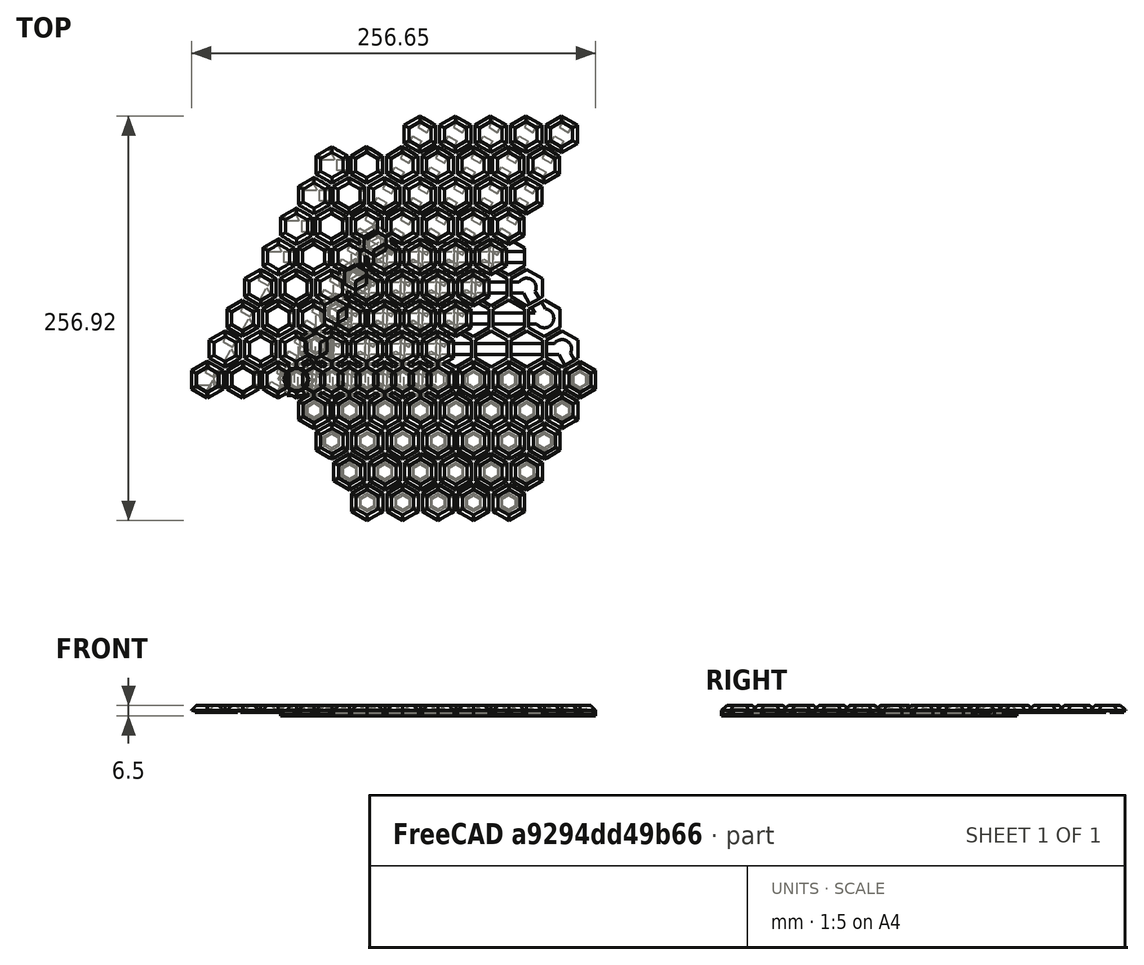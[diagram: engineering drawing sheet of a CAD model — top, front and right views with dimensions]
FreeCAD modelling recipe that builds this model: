
FCSTD DOCUMENT  (FreeCAD 0.21R33771 (Git))
Label: WearableHexLattice
License: All rights reserved
LicenseURL: http://en.wikipedia.org/wiki/All_rights_reserved
objects: Part::FeaturePython×65, Sketcher::SketchObject×16, PartDesign::Pad×12, PartDesign::Body×9, PartDesign::ShapeBinder×6, PartDesign::Pocket×4, Part::Mirroring×4, App::Part×4, PartDesign::FeatureBase×2, Part::Compound×2, Part::MultiFuse×1, Part::Box×1, Part::Cut×1, Mesh::Feature×1, TechDraw::DrawSVGTemplate×1, TechDraw::DrawViewPart×1, TechDraw::DrawPage×1, Spreadsheet::Sheet×1
note: 139 computed .brp shape members not serialized (recipe doc carries the construction recipe); baked Part::Feature solids carry a one-line shape summary decoded from their .brp

FEATURE [Sketcher::SketchObject] Sketch
  FullyConstrained = true
  MapMode = 5
  expr: Constraints[19] = 10 mm * 2 / sqrt(3)
  sketch-geometry (7):
    g0: LineSegment StartX=-11.547 StartY=0 StartZ=0 EndX=-5.7735 EndY=-10 EndZ=0
    g1: LineSegment StartX=-5.7735 StartY=-10 StartZ=0 EndX=5.7735 EndY=-10 EndZ=0
    g2: LineSegment StartX=5.7735 StartY=-10 StartZ=0 EndX=11.547 EndY=1.41807e-11 EndZ=0
    g3: LineSegment StartX=11.547 StartY=1.41807e-11 StartZ=0 EndX=5.7735 EndY=10 EndZ=0
    g4: LineSegment StartX=5.7735 StartY=10 StartZ=0 EndX=-5.7735 EndY=10 EndZ=0
    g5: LineSegment StartX=-5.7735 StartY=10 StartZ=0 EndX=-11.547 EndY=0 EndZ=0
    g6: Circle CenterX=0 CenterY=0 CenterZ=0 NormalX=0 NormalY=0 NormalZ=1 AngleXU=0 Radius=11.547
  constraints (16):
    c: Coincident(g0,g1)
    c: Coincident(g1,g2)
    c: Coincident(g2,g3)
    c: Coincident(g3,g4)
    c: Coincident(g4,g5)
    c: Coincident(g5,g0)
    c: Equal(g0, g1-g5) x5
    c: PointOnObject(g0,g6)
    c: PointOnObject(g1,g6)
    c: PointOnObject(g2,g6)
    c: PointOnObject(g3,g6)
    c: PointOnObject(g4,g6)
    c: PointOnObject(g5,g6)
    c: Coincident(g6,g-1)
    c: PointOnObject(g5,g-1)
    c: DistanceX(g4,g4) = 11.547
FEATURE [PartDesign::Pad] Pad
  Direction = (0,0,1)
  Length = 3
  Length2 = 10
  Profile = -> Sketch
  ReferenceAxis = -> Sketch [N_Axis]
  TaperAngle = -45
  Type = 0
FEATURE [PartDesign::Pad] Pad001
  BaseFeature = -> Pad
  Direction = (0,0,1)
  Length = 3.5
  Length2 = 10
  Profile = -> Sketch
  ReferenceAxis = -> Sketch [N_Axis]
  Reversed = true
  Type = 0
FEATURE [Part::MultiFuse] Fusion
  Placement = pos=(0,0,0) rot=(0,0,1;0.523599rad)
  Shapes = -> [Pad001,Pad]
FEATURE [PartDesign::FeatureBase] BaseFeature
  BaseFeature = -> Fusion
FEATURE [Sketcher::SketchObject] Sketch002
  AttachmentOffset = pos=(0,0,-2) rot=(0,0,1;0.523599rad)
  FullyConstrained = true
  MapMode = 5
  Placement = pos=(0,0,-2) rot=(0,0,1;0.523599rad)
  Support = -> [XY_Plane]
  sketch-geometry (7):
    g0: LineSegment StartX=0 StartY=8 StartZ=0 EndX=-6.9282 EndY=4 EndZ=0
    g1: LineSegment StartX=-6.9282 StartY=4 StartZ=0 EndX=-6.9282 EndY=-4 EndZ=0
    g2: LineSegment StartX=-6.9282 StartY=-4 StartZ=0 EndX=0 EndY=-8 EndZ=0
    g3: LineSegment StartX=0 StartY=-8 StartZ=0 EndX=6.9282 EndY=-4 EndZ=0
    g4: LineSegment StartX=6.9282 StartY=-4 StartZ=0 EndX=6.9282 EndY=4 EndZ=0
    g5: LineSegment StartX=6.9282 StartY=4 StartZ=0 EndX=0 EndY=8 EndZ=0
    g6: Circle CenterX=0 CenterY=0 CenterZ=0 NormalX=0 NormalY=0 NormalZ=1 AngleXU=0 Radius=8
  constraints (16):
    c: Coincident(g0,g1)
    c: Coincident(g1,g2)
    c: Coincident(g2,g3)
    c: Coincident(g3,g4)
    c: Coincident(g4,g5)
    c: Coincident(g5,g0)
    c: Equal(g0, g1-g5) x5
    c: PointOnObject(g0,g6)
    c: PointOnObject(g1,g6)
    c: PointOnObject(g2,g6)
    c: PointOnObject(g3,g6)
    c: PointOnObject(g4,g6)
    c: PointOnObject(g5,g6)
    c: Coincident(g6,g-1)
    c: PointOnObject(g5,g-2)
    c: DistanceY(g4,g4) = 8
FEATURE [PartDesign::Pocket] Pocket
  BaseFeature = -> BaseFeature
  Direction = (0,0,-1)
  Length = 3
  Length2 = 5
  Profile = -> Sketch002
  ReferenceAxis = -> Sketch002 [N_Axis]
  Reversed = true
  TaperAngle = -45
  Type = 0
FEATURE [PartDesign::Body] Body  label="Cell"
  BaseFeature = -> Fusion
  Group = -> [BaseFeature,Sketch,Sketch002,Pocket]
  Origin = -> Origin
  Tip = -> Pocket
FEATURE [Sketcher::SketchObject] Sketch001
  FullyConstrained = true
  MapMode = 2
  Support = -> [Body]
  sketch-geometry (15):
    g0: LineSegment StartX=180 StartY=-1.42e-14 StartZ=0 EndX=135 EndY=77.9423 EndZ=0
    g1: LineSegment StartX=135 StartY=77.9423 StartZ=0 EndX=45 EndY=77.9423 EndZ=0
    g2: LineSegment StartX=45 StartY=77.9423 StartZ=0 EndX=0 EndY=0 EndZ=0
    g3: LineSegment StartX=0 StartY=0 StartZ=0 EndX=45 EndY=-77.9423 EndZ=0
    g4: LineSegment StartX=45 StartY=-77.9423 StartZ=0 EndX=135 EndY=-77.9423 EndZ=0
    g5: LineSegment StartX=135 StartY=-77.9423 StartZ=0 EndX=180 EndY=-1.42e-14 EndZ=0
    g6: Circle CenterX=90 CenterY=-1.59e-14 CenterZ=0 NormalX=0 NormalY=0 NormalZ=1 AngleXU=0 Radius=90
    g7: LineSegment StartX=33.75 StartY=58.4567 StartZ=0 EndX=146.25 EndY=58.4567 EndZ=0
    g8: LineSegment StartX=22.5 StartY=38.9711 StartZ=0 EndX=157.5 EndY=38.9711 EndZ=0
    g9: LineSegment StartX=11.25 StartY=19.4856 StartZ=0 EndX=168.75 EndY=19.4856 EndZ=0
    g10: LineSegment StartX=45 StartY=77.9423 StartZ=0 EndX=33.75 EndY=58.4567 EndZ=0
    g11: LineSegment StartX=33.75 StartY=58.4567 StartZ=0 EndX=22.5 EndY=38.9711 EndZ=0
    g12: LineSegment StartX=22.5 StartY=38.9711 StartZ=0 EndX=11.25 EndY=19.4856 EndZ=0
    g13: LineSegment StartX=0 StartY=0 StartZ=0 EndX=180 EndY=-1.42e-14 EndZ=0
    g14: LineSegment StartX=11.25 StartY=19.4856 StartZ=0 EndX=0 EndY=0 EndZ=0
  constraints (39):
    c: Coincident(g0,g1)
    c: Coincident(g1,g2)
    c: Coincident(g2,g3)
    c: Coincident(g3,g4)
    c: Coincident(g4,g5)
    c: Coincident(g5,g0)
    c: Equal(g0, g1-g5) x5
    c: PointOnObject(g0,g6)
    c: PointOnObject(g1,g6)
    c: PointOnObject(g2,g6)
    c: PointOnObject(g3,g6)
    c: PointOnObject(g4,g6)
    c: PointOnObject(g5,g6)
    c: Horizontal(g1)
    c: DistanceX(g1,g1) = 90
    c: PointOnObject(g3,g-2)
    c: PointOnObject(g3,g-1)
    c: PointOnObject(g7,g2)
    c: PointOnObject(g7,g0)
    c: Horizontal(g7)
    c: PointOnObject(g8,g2)
    c: PointOnObject(g8,g0)
    c: Horizontal(g8)
    c: PointOnObject(g9,g2)
    c: PointOnObject(g9,g0)
    c: Horizontal(g9)
    c: Coincident(g10,g1)
    c: Coincident(g10,g7)
    c: Coincident(g11,g7)
    c: Coincident(g11,g8)
    c: Coincident(g12,g8)
    c: Coincident(g12,g9)
    c: Equal(g10,g11)
    c: Equal(g11,g12)
    c: Coincident(g13,g2)
    c: Coincident(g13,g0)
    c: Coincident(g14,g9)
    c: Coincident(g14,g2)
    c: Equal(g12,g14)
FEATURE [Part::Box] Box001  label="Cube"
  AttacherType = Attacher::AttachEngine3D
  Height = 2.5
  Length = 8
  Placement = pos=(-4,-10,-2.5) rot=(0,0,1;0rad)
  Support = -> [XY_Plane]
  Width = 20
FEATURE [Part::FeaturePython] Array  # Draft array (typed FeaturePython)
  AlwaysSyncPlacement = false
  Angle = 120
  ArrayType = 1
  Axis = (0,0,1)
  Base = -> Box001
  Center = (0,0,0)
  Count = 3
  ExpandArray = false
  Fuse = true
  IntervalAxis = (0,0,0)
  IntervalX = (50,0,0)
  IntervalY = (0,50,0)
  IntervalZ = (0,0,50)
  NumberCircles = 3
  NumberPolar = 3
  NumberX = 2
  NumberY = 2
  NumberZ = 1
  PlacementList = 3 placements: [(-4,-10,-2.5),(6.66025,-8.4641,-2.5),(10.6603,1.5359,-2.5)]
  RadialDistance = 50
  ScaleList = (3) [(1,1,1),(1,1,1),(1,1,1)]
  Symmetry = 1
  TangentialDistance = 25
FEATURE [Part::Cut] Cut
  Base = -> Body
  Placement = pos=(0,0,0) rot=(0,0,1;0.523599rad)
  Refine = true
  Tool = -> Array
FEATURE [Part::FeaturePython] Clone  label="Cell001"  # Draft clone (typed FeaturePython)
  AttacherType = Attacher::AttachEngine3D
  Fuse = false
  Objects = -> [Cut]
  Placement = pos=(12.5,21.6506,0) rot=(0,0,1;0.523599rad)
  Scale = (1,1,1)
  expr: .Placement.Base.x = 25 / 2
  expr: .Placement.Base.y = 25 * sqrt(3) / 2
FEATURE [Part::FeaturePython] Clone001  label="Cell002"  # Draft clone (typed FeaturePython)
  AttacherType = Attacher::AttachEngine3D
  Fuse = false
  Objects = -> [Cut]
  Placement = pos=(25,43.3013,0) rot=(0,0,1;0.523599rad)
  Scale = (1,1,1)
  expr: .Placement.Base.x = 50 / 2
  expr: .Placement.Base.y = 50 * sqrt(3) / 2
FEATURE [Part::FeaturePython] Clone002  label="Cell003"  # Draft clone (typed FeaturePython)
  AttacherType = Attacher::AttachEngine3D
  Fuse = false
  Objects = -> [Cut]
  Placement = pos=(37.5,64.9519,0) rot=(0,0,1;0.523599rad)
  Scale = (1,1,1)
  expr: .Placement.Base.x = 75 / 2
  expr: .Placement.Base.y = 75 * sqrt(3) / 2
FEATURE [Part::FeaturePython] Clone003  label="Cell004"  # Draft clone (typed FeaturePython)
  AttacherType = Attacher::AttachEngine3D
  Fuse = false
  Objects = -> [Cut]
  Placement = pos=(50,86.6025,0) rot=(0,0,1;0.523599rad)
  Scale = (1,1,1)
  expr: .Placement.Base.x = 100 / 2
  expr: .Placement.Base.y = 100 * sqrt(3) / 2
FEATURE [Part::FeaturePython] PathArray004  # WARN: FeaturePython — macro-defined, semantics opaque (R4)
  Align = false
  AlignMode = 0
  Base = -> Cut
  Count = 9
  EndOffset = 0
  ExtraTranslation = (0,0,0)
  ForceVertical = false
  PathObject = -> Sketch001
  PathSubelements = -> [Sketch001]
  StartOffset = 0
  TangentVector = (1,0,0)
  VerticalVector = (0,0,1)
FEATURE [Mesh::Feature] Mesh005
FEATURE [TechDraw::DrawSVGTemplate] Template
  EditableTexts = Designed_by_Name=Designed by Name; Drawing_number=Drawing number; FC-Date=Date; FC-SC=Scale; FC-SH=Sheet; FC-Title=Title; Subtitle=Subtitle; Weight=Weight
  Height = 210
  Orientation = 1
  Template = C:/Program Files/FreeCAD 0.21/data/Mod/TechDraw/Templates/A4_LandscapeTD.svg
  Width = 297
FEATURE [Part::FeaturePython] Clone004  label="Cut001"  # Draft clone (typed FeaturePython)
  AttacherType = Attacher::AttachEngine3D
  Fuse = false
  Objects = -> [Cut]
  Placement = pos=(0,0,0) rot=(0,0,1;0.523599rad)
  Scale = (1,1,1)
FEATURE [Part::FeaturePython] PathArray  # WARN: FeaturePython — macro-defined, semantics opaque (R4)
  Align = false
  AlignMode = 0
  Base = -> Clone004
  Count = 5
  EndOffset = 0
  ExtraTranslation = (0,0,0)
  ForceVertical = false
  PathObject = -> Sketch001
  PathSubelements = -> [Sketch001]
  StartOffset = 0
  TangentVector = (1,0,0)
  VerticalVector = (0,0,1)
FEATURE [Part::Mirroring] Part__Mirroring  label="PathArray (Mirror #1)"
  Base = (0,0,0)
  Normal = (0,1,0)
  Source = -> PathArray
FEATURE [Part::FeaturePython] Clone005  label="Cut002"  # Draft clone (typed FeaturePython)
  AttacherType = Attacher::AttachEngine3D
  Fuse = false
  Objects = -> [Cut]
  Placement = pos=(0,0,0) rot=(0,0,1;0.523599rad)
  Scale = (1,1,1)
FEATURE [Part::FeaturePython] PathArray001  # WARN: FeaturePython — macro-defined, semantics opaque (R4)
  Align = false
  AlignMode = 0
  Base = -> Clone005
  Count = 6
  EndOffset = 0
  ExtraTranslation = (0,0,0)
  ForceVertical = false
  PathObject = -> Sketch001
  PathSubelements = -> [Sketch001]
  StartOffset = 0
  TangentVector = (1,0,0)
  VerticalVector = (0,0,1)
FEATURE [Part::Mirroring] Part__Mirroring001  label="PathArray001 (Mirror #2)"
  Base = (0,0,0)
  Normal = (0,1,0)
  Source = -> PathArray001
FEATURE [Part::FeaturePython] Clone006  label="Cut003"  # Draft clone (typed FeaturePython)
  AttacherType = Attacher::AttachEngine3D
  Fuse = false
  Objects = -> [Cut]
  Placement = pos=(0,0,0) rot=(0,0,1;0.523599rad)
  Scale = (1,1,1)
FEATURE [Part::FeaturePython] PathArray002  # WARN: FeaturePython — macro-defined, semantics opaque (R4)
  Align = false
  AlignMode = 0
  Base = -> Clone006
  Count = 7
  EndOffset = 0
  ExtraTranslation = (0,0,0)
  ForceVertical = false
  PathObject = -> Sketch001
  PathSubelements = -> [Sketch001]
  StartOffset = 0
  TangentVector = (1,0,0)
  VerticalVector = (0,0,1)
FEATURE [Part::Mirroring] Part__Mirroring002  label="PathArray002 (Mirror #3)"
  Base = (0,0,0)
  Normal = (0,1,0)
  Source = -> PathArray002
FEATURE [Part::FeaturePython] Clone007  label="Cut004"  # Draft clone (typed FeaturePython)
  AttacherType = Attacher::AttachEngine3D
  Fuse = false
  Objects = -> [Cut]
  Placement = pos=(0,0,0) rot=(0,0,1;0.523599rad)
  Scale = (1,1,1)
FEATURE [Part::FeaturePython] PathArray003  # WARN: FeaturePython — macro-defined, semantics opaque (R4)
  Align = false
  AlignMode = 0
  Base = -> Clone007
  Count = 8
  EndOffset = 0
  ExtraTranslation = (0,0,0)
  ForceVertical = false
  PathObject = -> Sketch001
  PathSubelements = -> [Sketch001]
  StartOffset = 0
  TangentVector = (1,0,0)
  VerticalVector = (0,0,1)
FEATURE [Part::Mirroring] Part__Mirroring003  label="PathArray003 (Mirror #4)"
  Base = (0,0,0)
  Normal = (0,1,0)
  Source = -> PathArray003
FEATURE [App::Part] Part
  Group = -> [PathArray,PathArray001,PathArray002,PathArray003,PathArray004,Part__Mirroring,Part__Mirroring001,Part__Mirroring002,Part__Mirroring003]
  Origin = -> Origin001
FEATURE [TechDraw::DrawViewPart] View  label="Hex Lattice"
  CoarseView = false
  Direction = (0,0,1)
  Focus = 100
  HardHidden = false
  IsoCount = 0
  IsoHidden = false
  IsoVisible = false
  LockPosition = false
  Perspective = false
  Rotation = 0
  ScaleType = 0
  ScrubCount = 0
  SeamHidden = false
  SeamVisible = false
  SmoothHidden = false
  SmoothVisible = true
  Source = -> [PathArray004,Part__Mirroring,PathArray,Part__Mirroring001,PathArray001,Part__Mirroring002,PathArray002,Part__Mirroring003,PathArray003]
  X = 148.5
  XDirection = (1,0,0)
  Y = 105
FEATURE [TechDraw::DrawPage] Page
  KeepUpdated = true
  NextBalloonIndex = 1
  ProjectionType = 0
  Template = -> Template
  Views = -> [View]
FEATURE [Sketcher::SketchObject] Sketch003
  FullyConstrained = true
  MapMode = 5
  Support = -> [XY_Plane004]
  sketch-geometry (7):
    g0: LineSegment StartX=11.547 StartY=0 StartZ=0 EndX=5.7735 EndY=10 EndZ=0
    g1: LineSegment StartX=5.7735 StartY=10 StartZ=0 EndX=-5.7735 EndY=10 EndZ=0
    g2: LineSegment StartX=-5.7735 StartY=10 StartZ=0 EndX=-11.547 EndY=2.13e-14 EndZ=0
    g3: LineSegment StartX=-11.547 StartY=2.13e-14 StartZ=0 EndX=-5.7735 EndY=-10 EndZ=0
    g4: LineSegment StartX=-5.7735 StartY=-10 StartZ=0 EndX=5.7735 EndY=-10 EndZ=0
    g5: LineSegment StartX=5.7735 StartY=-10 StartZ=0 EndX=11.547 EndY=0 EndZ=0
    g6: Circle CenterX=0 CenterY=0 CenterZ=0 NormalX=0 NormalY=0 NormalZ=1 AngleXU=0 Radius=11.547
  constraints (16):
    c: Coincident(g0,g1)
    c: Coincident(g1,g2)
    c: Coincident(g2,g3)
    c: Coincident(g3,g4)
    c: Coincident(g4,g5)
    c: Coincident(g5,g0)
    c: Equal(g0, g1-g5) x5
    c: PointOnObject(g0,g6)
    c: PointOnObject(g1,g6)
    c: PointOnObject(g2,g6)
    c: PointOnObject(g3,g6)
    c: PointOnObject(g4,g6)
    c: PointOnObject(g5,g6)
    c: Coincident(g6,g-1)
    c: PointOnObject(g5,g-1)
    c: DistanceX(g1,g1) = 11.547
FEATURE [PartDesign::Pad] Pad002
  Direction = (0,0,1)
  Length = 3.5
  Length2 = 10
  Profile = -> Sketch003
  ReferenceAxis = -> Sketch003 [N_Axis]
  Reversed = true
  Type = 0
FEATURE [Sketcher::SketchObject] Sketch004
  ExternalGeometry = -> [Pad002]
  FullyConstrained = true
  MapMode = 5
  Support = -> [Pad002]
  sketch-geometry (4):
    g0: LineSegment StartX=-3.5 StartY=10 StartZ=0 EndX=3.5 EndY=10 EndZ=0
    g1: LineSegment StartX=3.5 StartY=10 StartZ=0 EndX=3.5 EndY=-10 EndZ=0
    g2: LineSegment StartX=3.5 StartY=-10 StartZ=0 EndX=-3.5 EndY=-10 EndZ=0
    g3: LineSegment StartX=-3.5 StartY=-10 StartZ=0 EndX=-3.5 EndY=10 EndZ=0
  constraints (11):
    c: Coincident(g0,g1)
    c: Coincident(g1,g2)
    c: Coincident(g2,g3)
    c: Coincident(g3,g0)
    c: Horizontal(g0)
    c: Horizontal(g2)
    c: Vertical(g1)
    c: Vertical(g3)
    c: PointOnObject(g0,g-3)
    c: Symmetric(g0,g2,g-1)
    c: DistanceX(g0,g0) = 7
FEATURE [PartDesign::Pocket] Pocket001
  BaseFeature = -> Pad002
  Direction = (0,0,-1)
  Length = 2
  Length2 = 5
  Profile = -> Sketch004
  ReferenceAxis = -> Sketch004 [N_Axis]
  Type = 0
FEATURE [PartDesign::Body] Body001  label="StraightBottom"
  Group = -> [Sketch003,Pad002,Sketch004,Pocket001]
  Origin = -> Origin004
  Tip = -> Pocket001
FEATURE [PartDesign::ShapeBinder] ShapeBinder
  Support = -> [Pad002]
  TraceSupport = false
FEATURE [Sketcher::SketchObject] Sketch005
  ExternalGeometry = -> [ShapeBinder]
  FullyConstrained = true
  MapMode = 5
  Support = -> [XY_Plane005]
  sketch-geometry (6):
    g0: LineSegment StartX=-5.7735 StartY=10 StartZ=0 EndX=5.7735 EndY=10 EndZ=0
    g1: LineSegment StartX=5.7735 StartY=10 StartZ=0 EndX=11.547 EndY=0 EndZ=0
    g2: LineSegment StartX=11.547 StartY=0 StartZ=0 EndX=5.7735 EndY=-10 EndZ=0
    g3: LineSegment StartX=5.7735 StartY=-10 StartZ=0 EndX=-5.7735 EndY=-10 EndZ=0
    g4: LineSegment StartX=-5.7735 StartY=-10 StartZ=0 EndX=-11.547 EndY=0 EndZ=0
    g5: LineSegment StartX=-11.547 StartY=0 StartZ=0 EndX=-5.7735 EndY=10 EndZ=0
  constraints (12):
    c: Coincident(g0,g-3)
    c: Coincident(g0,g-4)
    c: Coincident(g0,g1)
    c: Coincident(g1,g-5)
    c: Coincident(g1,g2)
    c: Coincident(g2,g-6)
    c: Coincident(g2,g3)
    c: Coincident(g3,g-7)
    c: Coincident(g3,g4)
    c: Coincident(g4,g-8)
    c: Coincident(g4,g5)
    c: Coincident(g5,g0)
FEATURE [PartDesign::Pad] Pad003
  Direction = (0,0,1)
  Length = 3
  Length2 = 10
  Profile = -> Sketch005
  ReferenceAxis = -> Sketch005 [N_Axis]
  TaperAngle = -45
  Type = 0
FEATURE [PartDesign::Body] Body002  label="Top"
  Group = -> [ShapeBinder,Sketch005,Pad003]
  Origin = -> Origin005
  Tip = -> Pad003
FEATURE [PartDesign::ShapeBinder] ShapeBinder001
  Support = -> [Pad002]
  TraceSupport = false
FEATURE [Sketcher::SketchObject] Sketch006
  ExternalGeometry = -> [ShapeBinder001]
  FullyConstrained = true
  MapMode = 5
  Support = -> [XY_Plane006]
  sketch-geometry (6):
    g0: LineSegment StartX=-5.7735 StartY=10 StartZ=0 EndX=5.7735 EndY=10 EndZ=0
    g1: LineSegment StartX=5.7735 StartY=10 StartZ=0 EndX=11.547 EndY=0 EndZ=0
    g2: LineSegment StartX=11.547 StartY=0 StartZ=0 EndX=5.7735 EndY=-10 EndZ=0
    g3: LineSegment StartX=5.7735 StartY=-10 StartZ=0 EndX=-5.7735 EndY=-10 EndZ=0
    g4: LineSegment StartX=-5.7735 StartY=-10 StartZ=0 EndX=-11.547 EndY=0 EndZ=0
    g5: LineSegment StartX=-11.547 StartY=0 StartZ=0 EndX=-5.7735 EndY=10 EndZ=0
  constraints (12):
    c: Coincident(g0,g-3)
    c: Coincident(g0,g-4)
    c: Coincident(g0,g1)
    c: Coincident(g1,g-5)
    c: Coincident(g1,g2)
    c: Coincident(g2,g-6)
    c: Coincident(g2,g3)
    c: Coincident(g3,g-7)
    c: Coincident(g3,g4)
    c: Coincident(g4,g-8)
    c: Coincident(g4,g5)
    c: Coincident(g5,g0)
FEATURE [PartDesign::Pad] Pad004
  Direction = (0,0,1)
  Length = 3.5
  Length2 = 10
  Profile = -> Sketch006
  ReferenceAxis = -> Sketch006 [N_Axis]
  Reversed = true
  Type = 0
FEATURE [Sketcher::SketchObject] Sketch007
  ExternalGeometry = -> [Pad004]
  FullyConstrained = true
  MapMode = 5
  Support = -> [XY_Plane006]
  sketch-geometry (10):
    g0: LineSegment StartX=-3.5 StartY=-10 StartZ=0 EndX=-3.5 EndY=-2.02073 EndZ=0
    g1: LineSegment StartX=-3.5 StartY=-2.02073 StartZ=0 EndX=-10.4102 EndY=1.96891 EndZ=0
    g2: LineSegment StartX=-6.91025 StartY=8.03109 StartZ=0 EndX=-2.47049 EndY=5.46779 EndZ=0
    g3: LineSegment StartX=3.5 StartY=-10 StartZ=0 EndX=-3.5 EndY=-10 EndZ=0
    g4: LineSegment StartX=-11.547 StartY=0 StartZ=0 EndX=-5.7735 EndY=10 EndZ=0
    g5: GeomPoint X=-8.66025 Y=5 Z=0
    g6: GeomPoint X=0 Y=-10 Z=0
    g7: LineSegment StartX=-10.4102 StartY=1.96891 StartZ=0 EndX=-6.91025 EndY=8.03109 EndZ=0
    g8: LineSegment StartX=3.5 StartY=-10 StartZ=0 EndX=3.5 EndY=-4.8734 EndZ=0
    g9: ArcOfCircle CenterX=0 CenterY=0 CenterZ=0 NormalX=0 NormalY=0 NormalZ=1 AngleXU=0 Radius=6 StartAngle=5.33522 EndAngle=8.27835
  constraints (23):
    c: Vertical(g0)
    c: Coincident(g0,g1)
    c: Coincident(g3,g0)
    c: Horizontal(g3)
    c: Coincident(g4,g-5)
    c: Coincident(g4,g-6)
    c: PointOnObject(g2,g4)
    c: Symmetric(g4,g4,g5)
    c: Symmetric(g2,g1,g5)
    c: Distance(g1,g2) = 7
    c: Parallel(g1,g2)
    c: Perpendicular(g4,g1)
    c: Symmetric(g-3,g-4,g6)
    c: Symmetric(g0,g3,g6)
    c: DistanceX(g3,g3) = 7
    c: Coincident(g7,g1)
    c: Coincident(g7,g2)
    c: Coincident(g8,g3)
    c: Vertical(g8)
    c: Coincident(g9,g-1)
    c: Coincident(g9,g2)
    c: Coincident(g9,g8)
    c: Diameter(g9) = 12
FEATURE [PartDesign::Pocket] Pocket002
  BaseFeature = -> Pad004
  Direction = (0,0,-1)
  Length = 2
  Length2 = 5
  Profile = -> Sketch007
  ReferenceAxis = -> Sketch007 [N_Axis]
  Type = 0
FEATURE [PartDesign::Body] Body003  label="60TurnBottom"
  Group = -> [ShapeBinder001,Sketch006,Pad004,Sketch007,Pocket002]
  Origin = -> Origin006
  Tip = -> Pocket002
FEATURE [PartDesign::ShapeBinder] ShapeBinder002
  Support = -> [Pad002]
  TraceSupport = false
FEATURE [Sketcher::SketchObject] Sketch008
  ExternalGeometry = -> [ShapeBinder002]
  FullyConstrained = true
  MapMode = 5
  Support = -> [XY_Plane007]
  sketch-geometry (10):
    g0: LineSegment StartX=3.5 StartY=-10 StartZ=0 EndX=3.5 EndY=-4.8734 EndZ=0
    g1: ArcOfCircle CenterX=-1.8e-15 CenterY=0 CenterZ=0 NormalX=0 NormalY=0 NormalZ=1 AngleXU=0 Radius=6 StartAngle=5.33522 EndAngle=9.32555
    g2: LineSegment StartX=-5.97049 StartY=0.59439 StartZ=0 EndX=-10.4103 EndY=-1.96891 EndZ=0
    g3: LineSegment StartX=-10.4103 StartY=-1.96891 StartZ=0 EndX=-6.91025 EndY=-8.03109 EndZ=0
    g4: LineSegment StartX=-6.91025 StartY=-8.03109 StartZ=0 EndX=-3.5 EndY=-6.06218 EndZ=0
    g5: LineSegment StartX=-3.5 StartY=-6.06218 StartZ=0 EndX=-3.5 EndY=-10 EndZ=0
    g6: LineSegment StartX=-3.5 StartY=-10 StartZ=0 EndX=3.5 EndY=-10 EndZ=0
    g7: LineSegment StartX=-5.7735 StartY=-10 StartZ=0 EndX=-1.8e-15 EndY=0 EndZ=0
    g8: GeomPoint X=-8.66025 Y=-5 Z=0
    g9: GeomPoint X=-4.01e-14 Y=-10 Z=0
  constraints (24):
    c: PointOnObject(g0,g-4)
    c: Vertical(g0)
    c: PointOnObject(g2,g-3)
    c: Coincident(g2,g3)
    c: Coincident(g3,g4)
    c: Coincident(g4,g5)
    c: PointOnObject(g5,g-4)
    c: Vertical(g5)
    c: Coincident(g5,g6)
    c: Coincident(g6,g0)
    c: Coincident(g7,g-1)
    c: PointOnObject(g4,g7)
    c: Perpendicular(g2,g3)
    c: Perpendicular(g3,g4)
    c: DistanceX(g6,g6) = 7
    c: Coincident(g1,g2)
    c: Coincident(g1,g0)
    c: Symmetric(g-3,g7,g8)
    c: Symmetric(g3,g2,g8)
    c: Symmetric(g7,g-4,g9)
    c: Symmetric(g0,g5,g9)
    c: Coincident(g1,g7)
    c: PointOnObject(g8,g-3)
    c: Diameter(g1) = 12
FEATURE [Sketcher::SketchObject] Sketch009
  ExternalGeometry = -> [ShapeBinder002]
  FullyConstrained = true
  MapMode = 2
  Support = -> [ShapeBinder002]
  sketch-geometry (6):
    g0: LineSegment StartX=-11.547 StartY=0 StartZ=0 EndX=-5.7735 EndY=10 EndZ=0
    g1: LineSegment StartX=-5.7735 StartY=10 StartZ=0 EndX=5.7735 EndY=10 EndZ=0
    g2: LineSegment StartX=5.7735 StartY=10 StartZ=0 EndX=11.547 EndY=0 EndZ=0
    g3: LineSegment StartX=11.547 StartY=0 StartZ=0 EndX=5.7735 EndY=-10 EndZ=0
    g4: LineSegment StartX=5.7735 StartY=-10 StartZ=0 EndX=-5.7735 EndY=-10 EndZ=0
    g5: LineSegment StartX=-5.7735 StartY=-10 StartZ=0 EndX=-11.547 EndY=0 EndZ=0
  constraints (12):
    c: Coincident(g-3,g0)
    c: Coincident(g0,g-3)
    c: Coincident(g0,g1)
    c: Coincident(g1,g-4)
    c: Coincident(g1,g2)
    c: Coincident(g2,g-4)
    c: Coincident(g2,g3)
    c: Coincident(g3,g-5)
    c: Coincident(g3,g4)
    c: Coincident(g4,g-5)
    c: Coincident(g4,g5)
    c: Coincident(g5,g0)
FEATURE [PartDesign::Pad] Pad005
  Direction = (0,0,1)
  Length = 3.5
  Length2 = 10
  Profile = -> Sketch009
  ReferenceAxis = -> Sketch009 [N_Axis]
  Reversed = true
  Type = 0
FEATURE [PartDesign::Pocket] Pocket003
  BaseFeature = -> Pad005
  Direction = (0,0,-1)
  Length = 2
  Length2 = 5
  Profile = -> Sketch008
  ReferenceAxis = -> Sketch008 [N_Axis]
  Type = 0
FEATURE [PartDesign::Body] Body004  label="120TurnBottom"
  Group = -> [ShapeBinder002,Sketch008,Sketch009,Pad005,Pocket003]
  Origin = -> Origin007
  Tip = -> Pocket003
FEATURE [PartDesign::ShapeBinder] ShapeBinder003
  Support = -> [Body002]
  TraceSupport = false
FEATURE [Sketcher::SketchObject] Sketch010
  ExternalGeometry = -> [ShapeBinder003]
  FullyConstrained = true
  MapMode = 2
  Support = -> [ShapeBinder003]
  sketch-geometry (6):
    g0: LineSegment StartX=-11.547 StartY=0 StartZ=0 EndX=-5.7735 EndY=10 EndZ=0
    g1: LineSegment StartX=-5.7735 StartY=10 StartZ=0 EndX=5.7735 EndY=10 EndZ=0
    g2: LineSegment StartX=5.7735 StartY=10 StartZ=0 EndX=11.547 EndY=0 EndZ=0
    g3: LineSegment StartX=11.547 StartY=0 StartZ=0 EndX=5.7735 EndY=-10 EndZ=0
    g4: LineSegment StartX=5.7735 StartY=-10 StartZ=0 EndX=-5.7735 EndY=-10 EndZ=0
    g5: LineSegment StartX=-5.7735 StartY=-10 StartZ=0 EndX=-11.547 EndY=0 EndZ=0
  constraints (12):
    c: Coincident(g0,g-8)
    c: Coincident(g0,g-3)
    c: Coincident(g0,g1)
    c: Coincident(g1,g-4)
    c: Coincident(g1,g2)
    c: Coincident(g2,g-5)
    c: Coincident(g2,g3)
    c: Coincident(g3,g-6)
    c: Coincident(g3,g4)
    c: Coincident(g4,g-7)
    c: Coincident(g4,g5)
    c: Coincident(g5,g0)
FEATURE [PartDesign::Pad] Pad006
  Direction = (0,0,1)
  Length = 3
  Length2 = 10
  Profile = -> Sketch010
  ReferenceAxis = -> Sketch010 [N_Axis]
  TaperAngle = -45
  Type = 0
FEATURE [Sketcher::SketchObject] Sketch011
  ExternalGeometry = -> [Pad006]
  FullyConstrained = true
  MapMode = 5
  Support = -> [XY_Plane008]
  sketch-geometry (8):
    g0: LineSegment StartX=-3.25 StartY=10 StartZ=0 EndX=3.25 EndY=10 EndZ=0
    g1: LineSegment StartX=3.25 StartY=10 StartZ=0 EndX=3.25 EndY=3.25 EndZ=0
    g2: LineSegment StartX=3.25 StartY=3.25 StartZ=0 EndX=-3.25 EndY=3.25 EndZ=0
    g3: LineSegment StartX=-3.25 StartY=3.25 StartZ=0 EndX=-3.25 EndY=10 EndZ=0
    g4: LineSegment StartX=-3.25 StartY=-10 StartZ=0 EndX=3.25 EndY=-10 EndZ=0
    g5: LineSegment StartX=3.25 StartY=-10 StartZ=0 EndX=3.25 EndY=-3.25 EndZ=0
    g6: LineSegment StartX=3.25 StartY=-3.25 StartZ=0 EndX=-3.25 EndY=-3.25 EndZ=0
    g7: LineSegment StartX=-3.25 StartY=-3.25 StartZ=0 EndX=-3.25 EndY=-10 EndZ=0
  constraints (23):
    c: Coincident(g0,g1)
    c: Coincident(g1,g2)
    c: Coincident(g2,g3)
    c: Coincident(g3,g0)
    c: Horizontal(g0)
    c: Horizontal(g2)
    c: Vertical(g1)
    c: Vertical(g3)
    c: PointOnObject(g0,g-3)
    c: Coincident(g4,g5)
    c: Coincident(g5,g6)
    c: Coincident(g6,g7)
    c: Coincident(g7,g4)
    c: Horizontal(g4)
    c: Horizontal(g6)
    c: Vertical(g5)
    c: Vertical(g7)
    c: PointOnObject(g4,g-4)
    c: Vertical(g2,g6)
    c: Vertical(g1,g5)
    c: Symmetric(g6,g1,g-1)
    c: DistanceX(g4,g4) = 6.5
    c: DistanceY(g6,g2) = 6.5
FEATURE [PartDesign::Pad] Pad007
  BaseFeature = -> Pad006
  Direction = (0,0,1)
  Length = 1.5
  Length2 = 10
  Profile = -> Sketch011
  Reversed = true
  Type = 0
FEATURE [PartDesign::Body] Body005  label="StraightTop"
  Group = -> [ShapeBinder003,Sketch010,Pad006,Sketch011,Pad007]
  Origin = -> Origin008
  Tip = -> Pad007
FEATURE [PartDesign::ShapeBinder] ShapeBinder004
  Support = -> [Pad003]
  TraceSupport = false
FEATURE [Sketcher::SketchObject] Sketch012
  ExternalGeometry = -> [ShapeBinder004]
  FullyConstrained = true
  MapMode = 5
  Support = -> [XY_Plane009]
  sketch-geometry (6):
    g0: LineSegment StartX=-11.547 StartY=0 StartZ=0 EndX=-5.7735 EndY=10 EndZ=0
    g1: LineSegment StartX=-5.7735 StartY=10 StartZ=0 EndX=5.7735 EndY=10 EndZ=0
    g2: LineSegment StartX=5.7735 StartY=10 StartZ=0 EndX=11.547 EndY=0 EndZ=0
    g3: LineSegment StartX=11.547 StartY=0 StartZ=0 EndX=5.7735 EndY=-10 EndZ=0
    g4: LineSegment StartX=5.7735 StartY=-10 StartZ=0 EndX=-5.7735 EndY=-10 EndZ=0
    g5: LineSegment StartX=-5.7735 StartY=-10 StartZ=0 EndX=-11.547 EndY=0 EndZ=0
  constraints (12):
    c: Coincident(g0,g-8)
    c: Coincident(g0,g-3)
    c: Coincident(g0,g1)
    c: Coincident(g1,g-4)
    c: Coincident(g1,g2)
    c: Coincident(g2,g-5)
    c: Coincident(g2,g3)
    c: Coincident(g3,g-6)
    c: Coincident(g3,g4)
    c: Coincident(g4,g-7)
    c: Coincident(g4,g5)
    c: Coincident(g5,g0)
FEATURE [PartDesign::Pad] Pad008
  Direction = (0,0,1)
  Length = 3
  Length2 = 10
  Profile = -> Sketch012
  ReferenceAxis = -> Sketch012 [N_Axis]
  TaperAngle = -45
  Type = 0
FEATURE [Sketcher::SketchObject] Sketch013
  ExternalGeometry = -> [Sketch012]
  FullyConstrained = true
  MapMode = 5
  Support = -> [XY_Plane009]
  sketch-geometry (12):
    g0: LineSegment StartX=-11.547 StartY=0 StartZ=0 EndX=-5.7735 EndY=10 EndZ=0
    g1: LineSegment StartX=-5.7735 StartY=-10 StartZ=0 EndX=5.7735 EndY=-10 EndZ=0
    g2: LineSegment StartX=-3.5 StartY=-10 StartZ=0 EndX=3.5 EndY=-10 EndZ=0
    g3: LineSegment StartX=3.5 StartY=-10 StartZ=0 EndX=3.5 EndY=-3.5 EndZ=0
    g4: LineSegment StartX=3.5 StartY=-3.5 StartZ=0 EndX=-3.5 EndY=-3.5 EndZ=0
    g5: LineSegment StartX=-3.5 StartY=-3.5 StartZ=0 EndX=-3.5 EndY=-10 EndZ=0
    g6: GeomPoint X=0 Y=-10 Z=0
    g7: LineSegment StartX=-10.4102 StartY=1.96891 StartZ=0 EndX=-6.91025 EndY=8.03109 EndZ=0
    g8: LineSegment StartX=-6.91025 StartY=8.03109 StartZ=0 EndX=-3.5 EndY=6.06218 EndZ=0
    g9: LineSegment StartX=-3.5 StartY=6.06218 StartZ=0 EndX=-3.5 EndY=-2.02073 EndZ=0
    g10: LineSegment StartX=-3.5 StartY=-2.02073 StartZ=0 EndX=-10.4102 EndY=1.96891 EndZ=0
    g11: GeomPoint X=-8.66025 Y=5 Z=0
  constraints (29):
    c: Coincident(g0,g-3)
    c: Coincident(g0,g-4)
    c: Coincident(g1,g-8)
    c: Coincident(g1,g-7)
    c: Coincident(g2,g3)
    c: Coincident(g3,g4)
    c: Coincident(g4,g5)
    c: Coincident(g5,g2)
    c: Horizontal(g2)
    c: Horizontal(g4)
    c: Vertical(g3)
    c: Vertical(g5)
    c: PointOnObject(g2,g1)
    c: DistanceX(g2,g2) = 7
    c: PointOnObject(g6,g-2)
    c: Symmetric(g2,g2,g6)
    c: DistanceY(g4,g-1) = 3.5
    c: PointOnObject(g7,g0)
    c: Coincident(g7,g8)
    c: Coincident(g8,g9)
    c: Coincident(g9,g10)
    c: Coincident(g10,g7)
    c: Symmetric(g0,g0,g11)
    c: Symmetric(g7,g7,g11)
    c: Perpendicular(g8,g7)
    c: Parallel(g8,g10)
    c: Distance(g7,g7) = 7
    c: Vertical(g9)
    c: DistanceX(g9,g-1) = 3.5
FEATURE [PartDesign::Pad] Pad009
  BaseFeature = -> Pad008
  Direction = (0,0,1)
  Length = 1.5
  Length2 = 10
  Profile = -> Sketch013
  ReferenceAxis = -> Sketch013 [N_Axis]
  Reversed = true
  Type = 0
FEATURE [PartDesign::Body] Body006  label="60TurnTop"
  Group = -> [ShapeBinder004,Sketch012,Pad008,Sketch013,Pad009]
  Origin = -> Origin009
  Tip = -> Pad009
FEATURE [PartDesign::ShapeBinder] ShapeBinder005
  Support = -> [Pad003]
  TraceSupport = false
FEATURE [Sketcher::SketchObject] Sketch014
  ExternalGeometry = -> [ShapeBinder005]
  FullyConstrained = true
  MapMode = 5
  Support = -> [XY_Plane010]
  sketch-geometry (6):
    g0: LineSegment StartX=-11.547 StartY=0 StartZ=0 EndX=-5.7735 EndY=10 EndZ=0
    g1: LineSegment StartX=-5.7735 StartY=10 StartZ=0 EndX=5.7735 EndY=10 EndZ=0
    g2: LineSegment StartX=5.7735 StartY=10 StartZ=0 EndX=11.547 EndY=0 EndZ=0
    g3: LineSegment StartX=11.547 StartY=0 StartZ=0 EndX=5.7735 EndY=-10 EndZ=0
    g4: LineSegment StartX=5.7735 StartY=-10 StartZ=0 EndX=-5.7735 EndY=-10 EndZ=0
    g5: LineSegment StartX=-5.7735 StartY=-10 StartZ=0 EndX=-11.547 EndY=0 EndZ=0
  constraints (12):
    c: Coincident(g0,g-8)
    c: Coincident(g0,g-3)
    c: Coincident(g0,g1)
    c: Coincident(g1,g-4)
    c: Coincident(g1,g2)
    c: Coincident(g2,g-5)
    c: Coincident(g2,g3)
    c: Coincident(g3,g-6)
    c: Coincident(g3,g4)
    c: Coincident(g4,g-7)
    c: Coincident(g4,g5)
    c: Coincident(g5,g0)
FEATURE [PartDesign::Pad] Pad010
  Direction = (0,0,1)
  Length = 3
  Length2 = 10
  Profile = -> Sketch014
  ReferenceAxis = -> Sketch014 [N_Axis]
  TaperAngle = -45
  Type = 0
FEATURE [Sketcher::SketchObject] Sketch015
  ExternalGeometry = -> [Pad010]
  FullyConstrained = true
  MapMode = 5
  Support = -> [XY_Plane010]
  sketch-geometry (17):
    g0: LineSegment StartX=-5.7735 StartY=-10 StartZ=0 EndX=0 EndY=0 EndZ=0
    g1: LineSegment StartX=-3.25 StartY=-10 StartZ=0 EndX=-3.25 EndY=-8 EndZ=0
    g2: ArcOfCircle CenterX=-2.25 CenterY=-8 CenterZ=0 NormalX=0 NormalY=0 NormalZ=1 AngleXU=0 Radius=1 StartAngle=1.5708 EndAngle=3.14159
    g3: LineSegment StartX=-2.25 StartY=-7 StartZ=0 EndX=2.25 EndY=-7 EndZ=0
    g4: ArcOfCircle CenterX=2.25 CenterY=-8 CenterZ=0 NormalX=0 NormalY=0 NormalZ=1 AngleXU=0 Radius=1 StartAngle=1e-16 EndAngle=1.5708
    g5: LineSegment StartX=3.25 StartY=-8 StartZ=0 EndX=3.25 EndY=-10 EndZ=0
    g6: LineSegment StartX=3.25 StartY=-10 StartZ=0 EndX=-3.25 EndY=-10 EndZ=0
    g7: LineSegment StartX=-10.2852 StartY=-2.18542 StartZ=0 EndX=-8.5532 EndY=-1.18542 EndZ=0
    g8: ArcOfCircle CenterX=-8.0532 CenterY=-2.05144 CenterZ=0 NormalX=0 NormalY=0 NormalZ=1 AngleXU=0 Radius=1 StartAngle=0.523599 EndAngle=2.0944
    g9: LineSegment StartX=-7.18717 StartY=-1.55144 StartZ=0 EndX=-4.93717 EndY=-5.44855 EndZ=0
    g10: ArcOfCircle CenterX=-5.8032 CenterY=-5.94855 CenterZ=0 NormalX=0 NormalY=0 NormalZ=1 AngleXU=0 Radius=1 StartAngle=5.23599 EndAngle=6.80678
    g11: LineSegment StartX=-5.3032 StartY=-6.81458 StartZ=0 EndX=-7.03525 EndY=-7.81458 EndZ=0
    g12: LineSegment StartX=-7.03525 StartY=-7.81458 StartZ=0 EndX=-10.2852 EndY=-2.18542 EndZ=0
    g13: GeomPoint X=0 Y=-10 Z=0
    g14: GeomPoint X=-4.04145 Y=-7 Z=0
    g15: GeomPoint X=-8.66025 Y=-5 Z=0
    g16: LineSegment StartX=-8.66025 StartY=-5 StartZ=0 EndX=0 EndY=0 EndZ=0
  constraints (42):
    c: Coincident(g0,g-4)
    c: Coincident(g0,g-1)
    c: PointOnObject(g1,g-4)
    c: Vertical(g1)
    c: Tangent(g1,g2) = 1.5708
    c: Coincident(g2,g3)
    c: Horizontal(g3)
    c: Tangent(g3,g4) = 1.5708
    c: Coincident(g4,g5)
    c: PointOnObject(g5,g-4)
    c: Vertical(g5)
    c: Coincident(g5,g6)
    c: Coincident(g6,g1)
    c: PointOnObject(g7,g-3)
    c: Tangent(g7,g8) = 1.5708
    c: Tangent(g9,g10) = 1.5708
    c: PointOnObject(g11,g-3)
    c: Coincident(g11,g12)
    c: Coincident(g12,g7)
    c: Vertical(g2,g2)
    c: Horizontal(g4,g4)
    c: Equal(g4,g2)
    c: Radius(g4) = 1
    c: PointOnObject(g13,g-2)
    c: Symmetric(g1,g5,g13)
    c: DistanceX(g6,g6) = 6.5
    c: PointOnObject(g14,g0)
    c: PointOnObject(g14,g3)
    c: Parallel(g9,g12)
    c: Parallel(g7,g11)
    c: Perpendicular(g12,g7)
    c: Tangent(g8,g9) = 1.5708
    c: Tangent(g10,g11) = 1.5708
    c: Equal(g10,g2)
    c: Equal(g10,g8)
    c: Equal(g12,g6)
    c: PointOnObject(g14,g9)
    c: Symmetric(g11,g7,g15)
    c: Coincident(g16,g15)
    c: Coincident(g16,g0)
    c: Angle(g-2,g16) = 2.0944
    c: DistanceY(g13,g2) = 3
FEATURE [PartDesign::Pad] Pad011
  BaseFeature = -> Pad010
  Direction = (0,0,1)
  Length = 1.5
  Length2 = 10
  Profile = -> Sketch015
  ReferenceAxis = -> Sketch015 [N_Axis]
  Reversed = true
  Type = 0
FEATURE [PartDesign::Body] Body007  label="120TurnTop"
  Group = -> [ShapeBinder005,Sketch014,Pad010,Sketch015,Pad011]
  Origin = -> Origin010
  Tip = -> Pad011
FEATURE [App::Part] Part001  label="Singles"
  Group = -> [Body001,Body002,Body003,Body004,Body005,Body006,Body007]
  Origin = -> Origin002
FEATURE [PartDesign::FeatureBase] Clone008
  BaseFeature = -> Body004
FEATURE [PartDesign::Body] Body008
  Group = -> [Clone008]
  Origin = -> Origin012
  Placement = pos=(0,0,0) rot=(0,0,1;1.5708rad)
  Tip = -> Clone008
FEATURE [Part::FeaturePython] Clone009  label="StraightBottom001"  # Draft clone (typed FeaturePython)
  AttacherType = Attacher::AttachEngine3D
  Fuse = false
  Objects = -> [Body001]
  Placement = pos=(22.5,0,0) rot=(0,0,1;1.5708rad)
  Scale = (1,1,1)
  expr: .Placement.Base.x = <<Spreadsheet>>.LED_dist
FEATURE [Part::FeaturePython] LinearArray  # WARN: FeaturePython — macro-defined, semantics opaque (R4)
  Alignment = 0
  CellStart = A1
  Count = 6
  Dir = (1,2e-16,0)
  DirIsDriven = true
  DistributionLaw = 0
  DrivenProperty = 1
  EndInclusive = true
  ExposePlacement = false
  GeneratorMode = 1
  Link = -> Clone009
  LinkSubelement = Edge27
  MarkerShape = 1
  MarkerSize = 0
  NumElements = 6
  OrientMode = 1
  Placement = pos=(10,3.5,0) rot=(0,0,1;0rad)
  Point = (12.5,-3.5,0)
  PointIsDriven = true
  Reverse = true
  SpanEnd = 20
  SpanStart = 0
  Step = 22.5
  SubLink = -> Clone009 [Edge27]
  Type = lattice2LinearArray.LinearArray
  VSGVersion = 1
  Values = 0.0 | 22.5 | 45.0 | 67.5 | 90.0 | 112.5
  ValuesSource = 2
  isLattice = 1
  expr: Step = <<Spreadsheet>>.LED_dist
FEATURE [Part::FeaturePython] Populate  label="Populate LinearArray with StraightBottom001"  # WARN: FeaturePython — macro-defined, semantics opaque (R4)
  Copying = 0
  ExposePlacement = false
  MarkerShape = 1
  MarkerSize = 0
  NumElements = 0
  Object = -> Clone009
  OutputCompounding = 1
  PlacementsTo = -> LinearArray
  Referencing = 0
  Type = lattice2PopulateCopies.LatticePopulateCopies
  isLattice = 0
FEATURE [App::Part] Part002  label="BottomLattice"
  Group = -> [Body008,LinearArray,Clone009,Populate]
  Origin = -> Origin011
FEATURE [Part::FeaturePython] Clone010  label="120TurnBottom001"  # Draft clone (typed FeaturePython)
  AttacherType = Attacher::AttachEngine3D
  Fuse = false
  Objects = -> [Body004]
  Placement = pos=(180,0,0) rot=(0,0,-1;1.5708rad)
  Scale = (1,1,1)
  expr: .Placement.Base.x = 8 * <<Spreadsheet>>.LED_dist
FEATURE [Part::FeaturePython] Clone011  label="60TurnBottom001"  # Draft clone (typed FeaturePython)
  AttacherType = Attacher::AttachEngine3D
  Fuse = false
  Objects = -> [Body003]
  Placement = pos=(11.25,-19.4856,0) rot=(0,0,1;3.66519rad)
  Scale = (1,1,1)
  expr: .Placement.Base.x = <<Spreadsheet>>.LED_dist / 2
  expr: .Placement.Base.y = -<<Spreadsheet>>.LED_dist * sin(60)
FEATURE [Spreadsheet::Sheet] Spreadsheet
  cells = A1='LED distance; B1(LED_dist)=22.5
FEATURE [Part::FeaturePython] Clone012  label="StraightBottom002"  # Draft clone (typed FeaturePython)
  AttacherType = Attacher::AttachEngine3D
  Fuse = false
  Objects = -> [Body001]
  Placement = pos=(33.75,-19.4856,0) rot=(0,0,1;1.5708rad)
  Scale = (1,1,1)
  expr: .Placement.Base.x = <<Spreadsheet>>.LED_dist * 1.5
  expr: .Placement.Base.y = -<<Spreadsheet>>.LED_dist * sin(60)
FEATURE [Part::FeaturePython] LinearArray001  # WARN: FeaturePython — macro-defined, semantics opaque (R4)
  Alignment = 0
  CellStart = A1
  Count = 5
  Dir = (1,3e-16,0)
  DirIsDriven = true
  DistributionLaw = 0
  DrivenProperty = 1
  EndInclusive = true
  ExposePlacement = false
  GeneratorMode = 1
  Link = -> Clone012
  LinkSubelement = Edge16
  MarkerShape = 1
  MarkerSize = 0
  NumElements = 5
  OrientMode = 1
  Placement = pos=(-1.25,16,0) rot=(0,0,1;0rad)
  Point = (23.75,-15.9856,0)
  PointIsDriven = true
  Reverse = false
  SpanEnd = 20
  SpanStart = 0
  Step = 22.5
  SubLink = -> Clone012 [Edge16]
  Type = lattice2LinearArray.LinearArray
  VSGVersion = 1
  Values = 0.0 | 22.5 | 45.0 | 67.5 | 90.0
  ValuesSource = 2
  isLattice = 1
  expr: Step = <<Spreadsheet>>.LED_dist
FEATURE [Part::FeaturePython] Populate001  label="Populate LinearArray001 with StraightBottom002"  # WARN: FeaturePython — macro-defined, semantics opaque (R4)
  Copying = 0
  ExposePlacement = false
  MarkerShape = 1
  MarkerSize = 0
  NumElements = 0
  Object = -> Clone012
  OutputCompounding = 1
  PlacementsTo = -> LinearArray001
  Referencing = 0
  Type = lattice2PopulateCopies.LatticePopulateCopies
  isLattice = 0
FEATURE [Part::FeaturePython] Clone013  label="120TurnBottom002"  # Draft clone (typed FeaturePython)
  AttacherType = Attacher::AttachEngine3D
  Fuse = false
  Objects = -> [Body004]
  Placement = pos=(168.75,-19.4856,0) rot=(0,0,-1;0.523599rad)
  Scale = (1,1,1)
  expr: .Placement.Base.x = <<Spreadsheet>>.LED_dist * 7.5
  expr: .Placement.Base.y = -<<Spreadsheet>>.LED_dist * sin(60)
FEATURE [Part::FeaturePython] Clone014  label="120TurnBottom003"  # Draft clone (typed FeaturePython)
  AttacherType = Attacher::AttachEngine3D
  Fuse = false
  Objects = -> [Body004]
  Placement = pos=(22.5,-38.9711,0) rot=(0,0,1;1.5708rad)
  Scale = (1,1,1)
  expr: .Placement.Base.x = <<Spreadsheet>>.LED_dist
  expr: .Placement.Base.y = -2 * <<Spreadsheet>>.LED_dist * sin(60)
FEATURE [Part::FeaturePython] Clone015  label="StraightBottom003"  # Draft clone (typed FeaturePython)
  AttacherType = Attacher::AttachEngine3D
  Fuse = false
  Objects = -> [Body001]
  Placement = pos=(45,-38.9711,0) rot=(0,0,1;1.5708rad)
  Scale = (1,1,1)
  expr: .Placement.Base.x = 2 * <<Spreadsheet>>.LED_dist
  expr: .Placement.Base.y = -2 * <<Spreadsheet>>.LED_dist * sin(60)
FEATURE [Part::FeaturePython] LinearArray002  # WARN: FeaturePython — macro-defined, semantics opaque (R4)
  Alignment = 0
  CellStart = A1
  Count = 4
  Dir = (1,0,0)
  DirIsDriven = true
  DistributionLaw = 0
  DrivenProperty = 1
  EndInclusive = true
  ExposePlacement = false
  GeneratorMode = 1
  Link = -> Clone015
  LinkSubelement = Edge27
  MarkerShape = 1
  MarkerSize = 0
  NumElements = 4
  OrientMode = 1
  Placement = pos=(-12.5,42.4856,0) rot=(0,0,1;0rad)
  Point = (35,-42.4711,0)
  PointIsDriven = true
  Reverse = true
  SpanEnd = 20
  SpanStart = 0
  Step = 22.5
  SubLink = -> Clone015 [Edge27]
  Type = lattice2LinearArray.LinearArray
  VSGVersion = 1
  Values = 0.0 | 22.5 | 45.0 | 67.5
  ValuesSource = 2
  isLattice = 1
  expr: .Placement.Base.x = <<Spreadsheet>>.LED_dist - 35
  expr: .Placement.Base.y = 23 + <<Spreadsheet>>.LED_dist * sin(60)
  expr: Step = <<Spreadsheet>>.LED_dist
FEATURE [Part::FeaturePython] Populate002  label="Populate LinearArray002 with StraightBottom003"  # WARN: FeaturePython — macro-defined, semantics opaque (R4)
  Copying = 0
  ExposePlacement = false
  MarkerShape = 1
  MarkerSize = 0
  NumElements = 0
  Object = -> Clone015
  OutputCompounding = 1
  PlacementsTo = -> LinearArray002
  Referencing = 0
  Type = lattice2PopulateCopies.LatticePopulateCopies
  isLattice = 0
FEATURE [Part::FeaturePython] Clone016  label="60TurnBottom002"  # Draft clone (typed FeaturePython)
  AttacherType = Attacher::AttachEngine3D
  Fuse = false
  Objects = -> [Body003]
  Placement = pos=(157.5,-38.9711,0) rot=(0,0,-1;1.5708rad)
  Scale = (1,1,1)
  expr: .Placement.Base.x = 7 * <<Spreadsheet>>.LED_dist
  expr: .Placement.Base.y = -2 * <<Spreadsheet>>.LED_dist * sin(60)
FEATURE [Part::FeaturePython] Clone017  label="60TurnBottom003"  # Draft clone (typed FeaturePython)
  AttacherType = Attacher::AttachEngine3D
  Fuse = false
  Objects = -> [Clone011]
  Placement = pos=(33.75,-58.4611,0) rot=(0,0,1;3.66519rad)
  Scale = (1,1,1)
  expr: .Placement.Base.x = 11.25 + <<Spreadsheet>>.LED_dist
  expr: .Placement.Base.y = -19.49 - 2 * <<Spreadsheet>>.LED_dist * sin(60)
FEATURE [Part::FeaturePython] Clone018  label="StraightBottom004"  # Draft clone (typed FeaturePython)
  AttacherType = Attacher::AttachEngine3D
  Fuse = false
  Objects = -> [Clone015]
  Placement = pos=(56.25,-58.4556,0) rot=(0,0,1;1.5708rad)
  Scale = (1,1,1)
  expr: .Placement.Base.x = 45 + <<Spreadsheet>>.LED_dist / 2
  expr: .Placement.Base.y = -38.97 - <<Spreadsheet>>.LED_dist * sin(60)
FEATURE [Part::FeaturePython] LinearArray003  # WARN: FeaturePython — macro-defined, semantics opaque (R4)
  Alignment = 0
  CellStart = A1
  Count = 3
  Dir = (1,2e-16,0)
  DirIsDriven = true
  DistributionLaw = 0
  DrivenProperty = 1
  EndInclusive = true
  ExposePlacement = false
  GeneratorMode = 1
  Link = -> Clone009
  LinkSubelement = Edge16
  MarkerShape = 1
  MarkerSize = 0
  NumElements = 3
  OrientMode = 1
  Placement = pos=(10,-3.5,0) rot=(0,0,1;0rad)
  Point = (12.5,3.5,0)
  PointIsDriven = true
  Reverse = false
  SpanEnd = 20
  SpanStart = 0
  Step = 22.5
  SubLink = -> Clone009 [Edge16]
  Type = lattice2LinearArray.LinearArray
  VSGVersion = 1
  Values = 0.0 | 22.5 | 45.0
  ValuesSource = 2
  isLattice = 1
  expr: Step = <<Spreadsheet>>.LED_dist
FEATURE [Part::FeaturePython] Populate003  label="Populate LinearArray003 with StraightBottom004"  # WARN: FeaturePython — macro-defined, semantics opaque (R4)
  Copying = 0
  ExposePlacement = false
  MarkerShape = 1
  MarkerSize = 0
  NumElements = 0
  Object = -> Clone018
  OutputCompounding = 1
  PlacementsTo = -> LinearArray003
  Referencing = 0
  Type = lattice2PopulateCopies.LatticePopulateCopies
  isLattice = 0
FEATURE [Part::FeaturePython] Clone019  label="120TurnBottom004"  # Draft clone (typed FeaturePython)
  AttacherType = Attacher::AttachEngine3D
  Fuse = false
  Objects = -> [Clone013]
  Placement = pos=(146.25,-58.4611,0) rot=(0,0,-1;0.523599rad)
  Scale = (1,1,1)
  expr: .Placement.Base.x = 168.75 - <<Spreadsheet>>.LED_dist
  expr: .Placement.Base.y = -19.49 - 2 * sin(60) * <<Spreadsheet>>.LED_dist
FEATURE [Part::FeaturePython] Clone020  label="60TurnBottom004"  # Draft clone (typed FeaturePython)
  AttacherType = Attacher::AttachEngine3D
  Fuse = false
  Objects = -> [Clone016]
  Placement = pos=(135,-77.9411,0) rot=(0,0,-1;1.5708rad)
  Scale = (1,1,1)
  expr: .Placement.Base.x = 157.5 - <<Spreadsheet>>.LED_dist
  expr: .Placement.Base.y = -38.97 - 2 * sin(60) * <<Spreadsheet>>.LED_dist
FEATURE [Part::FeaturePython] Clone022  label="StraightBottom005"  # Draft clone (typed FeaturePython)
  AttacherType = Attacher::AttachEngine3D
  Fuse = false
  Objects = -> [Clone018]
  Placement = pos=(45,-77.9456,0) rot=(0,0,1;1.5708rad)
  Scale = (1,1,1)
  expr: .Placement.Base.x = 56.25 - <<Spreadsheet>>.LED_dist / 2
  expr: .Placement.Base.y = -58.46 - <<Spreadsheet>>.LED_dist * sin(60)
FEATURE [Part::FeaturePython] LinearArray004  # WARN: FeaturePython — macro-defined, semantics opaque (R4)
  Alignment = 0
  CellStart = A1
  Count = 3
  Dir = (1,2e-16,0)
  DirIsDriven = true
  DistributionLaw = 0
  DrivenProperty = 1
  EndInclusive = true
  ExposePlacement = false
  GeneratorMode = 1
  Link = -> Clone009
  LinkSubelement = Edge16
  MarkerShape = 1
  MarkerSize = 0
  NumElements = 3
  OrientMode = 1
  Placement = pos=(10,-3.5,0) rot=(0,0,1;0rad)
  Point = (12.5,3.5,0)
  PointIsDriven = true
  Reverse = false
  SpanEnd = 20
  SpanStart = 0
  Step = 22.5
  SubLink = -> Clone009 [Edge16]
  Type = lattice2LinearArray.LinearArray
  VSGVersion = 1
  Values = 0.0 | 22.5 | 45.0
  ValuesSource = 2
  isLattice = 1
  expr: Step = <<Spreadsheet>>.LED_dist
FEATURE [Part::FeaturePython] Populate004  label="Populate LinearArray004 with StraightBottom005"  # WARN: FeaturePython — macro-defined, semantics opaque (R4)
  Copying = 0
  ExposePlacement = false
  MarkerShape = 1
  MarkerSize = 0
  NumElements = 0
  Object = -> Clone022
  OutputCompounding = 1
  PlacementsTo = -> LinearArray004
  Referencing = 0
  Type = lattice2PopulateCopies.LatticePopulateCopies
  isLattice = 0
FEATURE [Part::FeaturePython] Clone023  label="StraightBottom006"  # Draft clone (typed FeaturePython)
  AttacherType = Attacher::AttachEngine3D
  Fuse = false
  Objects = -> [Clone022]
  Placement = pos=(45,-77.9456,0) rot=(0,0,1;1.5708rad)
  Scale = (1,1,1)
FEATURE [Part::FeaturePython] Clone024  label="Populate LinearArray004 with StraightBottom006"  # Draft clone (typed FeaturePython)
  AttacherType = Attacher::AttachEngine3D
  Fuse = false
  Objects = -> [Populate004]
  Scale = (1,1,1)
FEATURE [Part::FeaturePython] Clone025  label="60TurnBottom005"  # Draft clone (typed FeaturePython)
  AttacherType = Attacher::AttachEngine3D
  Fuse = false
  Objects = -> [Clone020]
  Placement = pos=(135,-77.9411,0) rot=(0,0,-1;1.5708rad)
  Scale = (1,1,1)
FEATURE [Part::FeaturePython] Clone026  label="120TurnBottom005"  # Draft clone (typed FeaturePython)
  AttacherType = Attacher::AttachEngine3D
  Fuse = false
  Objects = -> [Clone019]
  Placement = pos=(146.25,-58.4611,0) rot=(0,0,-1;0.523599rad)
  Scale = (1,1,1)
FEATURE [Part::FeaturePython] Clone027  label="StraightBottom007"  # Draft clone (typed FeaturePython)
  AttacherType = Attacher::AttachEngine3D
  Fuse = false
  Objects = -> [Clone018]
  Placement = pos=(56.25,-58.4556,0) rot=(0,0,1;1.5708rad)
  Scale = (1,1,1)
FEATURE [Part::FeaturePython] Clone028  label="Populate LinearArray003 with StraightBottom005"  # Draft clone (typed FeaturePython)
  AttacherType = Attacher::AttachEngine3D
  Fuse = false
  Objects = -> [Populate003]
  Scale = (1,1,1)
FEATURE [Part::FeaturePython] Clone029  label="60TurnBottom006"  # Draft clone (typed FeaturePython)
  AttacherType = Attacher::AttachEngine3D
  Fuse = false
  Objects = -> [Clone017]
  Placement = pos=(33.75,-58.4611,0) rot=(0,0,1;3.66519rad)
  Scale = (1,1,1)
FEATURE [Part::FeaturePython] Clone030  label="60TurnBottom007"  # Draft clone (typed FeaturePython)
  AttacherType = Attacher::AttachEngine3D
  Fuse = false
  Objects = -> [Clone016]
  Placement = pos=(157.5,-38.9711,0) rot=(0,0,-1;1.5708rad)
  Scale = (1,1,1)
FEATURE [Part::FeaturePython] Clone031  label="StraightBottom008"  # Draft clone (typed FeaturePython)
  AttacherType = Attacher::AttachEngine3D
  Fuse = false
  Objects = -> [Clone015]
  Placement = pos=(45,-38.9711,0) rot=(0,0,1;1.5708rad)
  Scale = (1,1,1)
FEATURE [Part::FeaturePython] Clone032  label="Populate LinearArray002 with StraightBottom004"  # Draft clone (typed FeaturePython)
  AttacherType = Attacher::AttachEngine3D
  Fuse = false
  Objects = -> [Populate002]
  Scale = (1,1,1)
FEATURE [Part::FeaturePython] Clone033  label="120TurnBottom006"  # Draft clone (typed FeaturePython)
  AttacherType = Attacher::AttachEngine3D
  Fuse = false
  Objects = -> [Clone014]
  Placement = pos=(22.5,-38.9711,0) rot=(0,0,1;1.5708rad)
  Scale = (1,1,1)
FEATURE [Part::FeaturePython] Clone034  label="120TurnBottom007"  # Draft clone (typed FeaturePython)
  AttacherType = Attacher::AttachEngine3D
  Fuse = false
  Objects = -> [Clone013]
  Placement = pos=(168.75,-19.4856,0) rot=(0,0,-1;0.523599rad)
  Scale = (1,1,1)
FEATURE [Part::FeaturePython] Clone035  label="StraightBottom009"  # Draft clone (typed FeaturePython)
  AttacherType = Attacher::AttachEngine3D
  Fuse = false
  Objects = -> [Clone012]
  Placement = pos=(33.75,-19.4856,0) rot=(0,0,1;1.5708rad)
  Scale = (1,1,1)
FEATURE [Part::FeaturePython] Clone036  label="Populate LinearArray001 with StraightBottom003"  # Draft clone (typed FeaturePython)
  AttacherType = Attacher::AttachEngine3D
  Fuse = false
  Objects = -> [Populate001]
  Scale = (1,1,1)
FEATURE [Part::FeaturePython] Clone037  label="60TurnBottom008"  # Draft clone (typed FeaturePython)
  AttacherType = Attacher::AttachEngine3D
  Fuse = false
  Objects = -> [Clone011]
  Placement = pos=(11.25,-19.4856,0) rot=(0,0,1;3.66519rad)
  Scale = (1,1,1)
FEATURE [Part::Compound] Compound
  Links = -> [Clone037,Clone036,Clone035,Clone034,Clone033,Clone032,Clone031,Clone030,Clone029,Clone028,Clone027,Clone026,Clone025,Clone024,Clone023]
  Placement = pos=(180,0,0) rot=(0,0,1;3.14159rad)
  expr: .Placement.Base.x = 8 * <<Spreadsheet>>.LED_dist
FEATURE [Part::Compound] Compound001  label="BottomPartToPrint"
  Links = -> [Compound,Clone022,Populate004,Clone020,Clone019,Clone018,Populate003,Clone017,Clone016,Clone015,Populate002,Clone014,Clone013,Clone012,Populate001,Clone011,Clone010,Populate,Clone009,Body008]
FEATURE [Part::FeaturePython] Clone038  label="StraightTop001"  # Draft clone (typed FeaturePython)
  AttacherType = Attacher::AttachEngine3D
  Fuse = false
  Objects = -> [Body005]
  Placement = pos=(0,0,0) rot=(0,0,1;1.5708rad)
  Scale = (1,1,1)
FEATURE [Part::FeaturePython] LinearArray005  # WARN: FeaturePython — macro-defined, semantics opaque (R4)
  Alignment = 0
  CellStart = A1
  Count = 5
  Dir = (1,0,0)
  DirIsDriven = true
  DistributionLaw = 0
  DrivenProperty = 1
  EndInclusive = true
  ExposePlacement = false
  GeneratorMode = 1
  MarkerShape = 1
  MarkerSize = 0
  NumElements = 5
  OrientMode = 1
  Point = (0,0,0)
  PointIsDriven = true
  Reverse = false
  SpanEnd = 100
  SpanStart = 0
  Step = 22.5
  Type = lattice2LinearArray.LinearArray
  VSGVersion = 1
  Values = 0.0 | 22.5 | 45.0 | 67.5 | 90.0
  ValuesSource = 2
  isLattice = 1
  expr: Step = <<Spreadsheet>>.LED_dist
FEATURE [Part::FeaturePython] LinearArray006  # WARN: FeaturePython — macro-defined, semantics opaque (R4)
  Alignment = 0
  CellStart = A1
  Count = 9
  Dir = (0.866025,0.5,0)
  DirIsDriven = true
  DistributionLaw = 0
  DrivenProperty = 1
  EndInclusive = true
  ExposePlacement = false
  GeneratorMode = 1
  Link = -> Clone038
  LinkSubelement = Edge10
  MarkerShape = 1
  MarkerSize = 0
  NumElements = 9
  OrientMode = 1
  Placement = pos=(0,0,0) rot=(0,0,1;0.523599rad)
  Point = (-10,5.7735,0)
  PointIsDriven = true
  Reverse = false
  SpanEnd = 11.547
  SpanStart = 0
  Step = 22.5
  SubLink = -> Clone038 [Edge10]
  Type = lattice2LinearArray.LinearArray
  VSGVersion = 1
  Values = 0.0 | 22.5 | 45.0 | 67.5 | 90.0 | 112.5 | 135.0 | 157.5 | 180.0
  ValuesSource = 2
  isLattice = 1
  expr: Step = <<Spreadsheet>>.LED_dist
FEATURE [Part::FeaturePython] Populate005  label="Populate LinearArray005 with LinearArray006"  # WARN: FeaturePython — macro-defined, semantics opaque (R4)
  Copying = 0
  ExposePlacement = false
  MarkerShape = 1
  MarkerSize = 0
  NumElements = 45
  Object = -> LinearArray006
  OutputCompounding = 0
  PlacementsTo = -> LinearArray005
  Referencing = 0
  Type = lattice2PopulateCopies.LatticePopulateCopies
  isLattice = 1
FEATURE [Part::FeaturePython] Populate006  label="Populate Populate LinearArray005 with LinearArray006 with StraightTop001"  # WARN: FeaturePython — macro-defined, semantics opaque (R4)
  Copying = 0
  ExposePlacement = false
  MarkerShape = 1
  MarkerSize = 0
  NumElements = 0
  Object = -> Clone038
  OutputCompounding = 1
  PlacementsTo = -> Populate005
  Referencing = 0
  Type = lattice2PopulateCopies.LatticePopulateCopies
  isLattice = 0
FEATURE [Part::FeaturePython] Clone039  label="120TurnTop001"  # Draft clone (typed FeaturePython)
  AttacherType = Attacher::AttachEngine3D
  Fuse = false
  Objects = -> [Body007]
  Placement = pos=(-33.75,0,0) rot=(0,0,1;1.5708rad)
  Scale = (1,1,1)
  expr: .Placement.Base.x = -1.5 * <<Spreadsheet>>.LED_dist
FEATURE [Part::FeaturePython] LinearArray007  # WARN: FeaturePython — macro-defined, semantics opaque (R4)
  Alignment = 0
  CellStart = A1
  Count = 8
  Dir = (-4.68e-14,1,0)
  DirIsDriven = true
  DistributionLaw = 0
  DrivenProperty = 1
  EndInclusive = true
  ExposePlacement = false
  GeneratorMode = 1
  Link = -> Clone039
  LinkSubelement = Edge5
  MarkerShape = 1
  MarkerSize = 0
  NumElements = 8
  OrientMode = 1
  Placement = pos=(23.6,12.35,0) rot=(0,0,-1;0.523599rad)
  Point = (-43.75,-5.7735,0)
  PointIsDriven = true
  Reverse = false
  SpanEnd = 11.547
  SpanStart = 0
  Step = 22.5
  SubLink = -> Clone039 [Edge5]
  Type = lattice2LinearArray.LinearArray
  VSGVersion = 1
  Values = 0.0 | 22.5 | 45.0 | 67.5 | 90.0 | 112.5 | 135.0 | 157.5
  ValuesSource = 2
  isLattice = 1
  expr: Step = <<Spreadsheet>>.LED_dist
FEATURE [Part::FeaturePython] Populate007  label="Populate LinearArray007 with 120TurnTop001"  # WARN: FeaturePython — macro-defined, semantics opaque (R4)
  Copying = 0
  ExposePlacement = false
  MarkerShape = 1
  MarkerSize = 0
  NumElements = 0
  Object = -> Clone039
  OutputCompounding = 1
  PlacementsTo = -> LinearArray007
  Referencing = 0
  Type = lattice2PopulateCopies.LatticePopulateCopies
  isLattice = 0
FEATURE [Part::FeaturePython] Clone040  label="60TurnTop001"  # Draft clone (typed FeaturePython)
  AttacherType = Attacher::AttachEngine3D
  Fuse = false
  Objects = -> [Body006]
  Placement = pos=(-56.25,0,0) rot=(0,0,1;1.5708rad)
  Scale = (1,1,1)
  expr: .Placement.Base.x = -2.5 * <<Spreadsheet>>.LED_dist
FEATURE [Part::FeaturePython] LinearArray008  # WARN: FeaturePython — macro-defined, semantics opaque (R4)
  Alignment = 0
  CellStart = A1
  Count = 4
  Dir = (-4.68e-14,1,0)
  DirIsDriven = true
  DistributionLaw = 0
  DrivenProperty = 1
  EndInclusive = true
  ExposePlacement = false
  GeneratorMode = 1
  Link = -> Clone040
  LinkSubelement = Edge10
  MarkerShape = 1
  MarkerSize = 0
  NumElements = 4
  OrientMode = 1
  Placement = pos=(31.74,20.59,0) rot=(0,0,-1;0.523599rad)
  Point = (-66.25,-5.7735,0)
  PointIsDriven = true
  Reverse = false
  SpanEnd = 11.547
  SpanStart = 0
  Step = 22.5
  SubLink = -> Clone040 [Edge10]
  Type = lattice2LinearArray.LinearArray
  VSGVersion = 1
  Values = 0.0 | 22.5 | 45.0 | 67.5
  ValuesSource = 2
  isLattice = 1
  expr: Step = <<Spreadsheet>>.LED_dist
FEATURE [Part::FeaturePython] Populate008  label="Populate LinearArray008 with 60TurnTop001"  # WARN: FeaturePython — macro-defined, semantics opaque (R4)
  Copying = 0
  ExposePlacement = false
  MarkerShape = 1
  MarkerSize = 0
  NumElements = 0
  Object = -> Clone040
  OutputCompounding = 1
  PlacementsTo = -> LinearArray008
  Referencing = 0
  Type = lattice2PopulateCopies.LatticePopulateCopies
  isLattice = 0
FEATURE [Part::FeaturePython] Clone041  label="60TurnTop002"  # Draft clone (typed FeaturePython)
  AttacherType = Attacher::AttachEngine3D
  Fuse = false
  Objects = -> [Body006]
  Placement = pos=(-11.25,77.9423,0) rot=(0,0,1;1.5708rad)
  Scale = (-1,1,1)
  expr: .Placement.Base.x = -<<Spreadsheet>>.LED_dist / 2
  expr: .Placement.Base.y = 4 * sin(60) * <<Spreadsheet>>.LED_dist
FEATURE [Part::FeaturePython] Populate009  label="Populate LinearArray008 with 60TurnTop002"  # WARN: FeaturePython — macro-defined, semantics opaque (R4)
  Copying = 0
  ExposePlacement = false
  MarkerShape = 1
  MarkerSize = 0
  NumElements = 0
  Object = -> Clone041
  OutputCompounding = 1
  PlacementsTo = -> LinearArray008
  Referencing = 1
  Type = lattice2PopulateCopies.LatticePopulateCopies
  isLattice = 0
FEATURE [App::Part] Part003  label="TopToPrint"
  Group = -> [LinearArray005,Clone038,LinearArray006,Populate005,Populate006,Clone039,LinearArray007,Populate007,Clone040,LinearArray008,Populate008,Clone041,Populate009]
  Origin = -> Origin013
  Placement = pos=(-112.5,0,0) rot=(1,0,0;3.14159rad)
  expr: .Placement.Base.x = -5 * <<Spreadsheet>>.LED_dist
